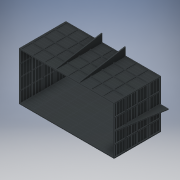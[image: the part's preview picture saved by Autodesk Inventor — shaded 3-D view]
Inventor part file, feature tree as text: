
AUTODESK INVENTOR PART (.ipt)
format: ipt  version: 2019 (Build 230136000, 136)  size: 1,216,512 bytes
history: native  units: in
note: dims shown in document units (in); Inventor stores cm internally (conversion verified against a paired STEP export)
features: sketch x10, extrude x9, pattern_linear x3, mirror x2, other x1, split x1
ambient origin geometry x8: Origin, YZ Plane, XZ Plane, XY Plane, X Axis, Y Axis, Z Axis, Center Point
bodies: Body1 (feature_tree)
feature tree (26):
  other  "Steel"
  extrude  "Extrusion1"  Depth=60.0in
  extrude  "Extrusion2"  Depth=119.79in
  split  "Split8"
  extrude  "Extrusion4"  Depth=59.895in TaperAngle=0.0deg
  extrude  "Extrusion5"  Depth=3.937in
  extrude  "Extrusion6"  Depth=3.937in
  pattern_linear  "Rectangular Pattern1"  Count1=10  [1 undecoded]
  extrude  "Extrusion7"  Depth=3.937in
  extrude  "Extrusion8"  Depth=3.937in
  pattern_linear  "Rectangular Pattern3"  Count1=10  [1 undecoded]
  extrude  "Extrusion9"  Depth=3.937in
  pattern_linear  "Rectangular Pattern4"  Count1=10  [1 undecoded]
  mirror  "Mirror1"
  extrude  "Extrusion10"  Depth=1.125in
  mirror  "Mirror2"
  sketch  "Sketch1"  dims[d0=120.0in d1=60.0in]
  sketch  "Sketch2"  dims[d2=60.0in d3=0.0in d4=119.79in]
  sketch  "Sketch12"  dims[d5=59.79in d6=59.895in d7=0.0in]
  sketch  "Sketch15"  dims[d46=3.937in d47=3.937in]
  sketch  "Sketch16"  dims[d48=3.937in d49=3.937in d50=3.937in]
  sketch  "Sketch17"  dims[d51=3.937in d52=3.937in]
  sketch  "Sketch18"  dims[d53=3.937in d54=3.937in d55=3.937in]
  sketch  "Sketch19"  dims[d56=3.937in d57=3.937in d58=3.937in]
  sketch  "Sketch20"  dims[d59=3.937in d65=1.125in]
  sketch  "Sketch21"  dims[d66=0.7874in d68=360.0deg d70=60.0in d71=0.0in d72=1.0in d73=1.9685in d75=14.75in d76=0.3937in d78=1.0in d80=1.0in d81=0.0in d82=1.0in d83=1.5748in d85=15.0in d86=1.5748in d88=14.75in d91=1.5748in d93=15.0in d94=0.3937in d96=1.0in d98=1.0in d99=0.0in d100=0.7874in d102=61.0in d103=1.0in d104=1.9685in d106=14.75in d107=0.3937in d109=1.0in d111=1.0in d112=0.0in d113=1.0in d114=0.7874in d116=15.0in d117=1.5748in d119=14.75in d122=0.7874in d124=15.0in d125=0.3937in d127=1.0in d129=1.0in d130=0.0in d134=1.0in d135=1.0in d136=0.7874in d138=121.0in d139=1.0in d141=1.0in d142=10.0in d143=1.0in d144=0.0in d145=0.7874in d147=30.0in d148=10.0in d149=1.0in d150=0.0in]
note: 3 required parameter values undecoded (feature->parameter linkage not recoverable at this tier; creation-order binding heuristic only, values carry confidence <= 0.55)
